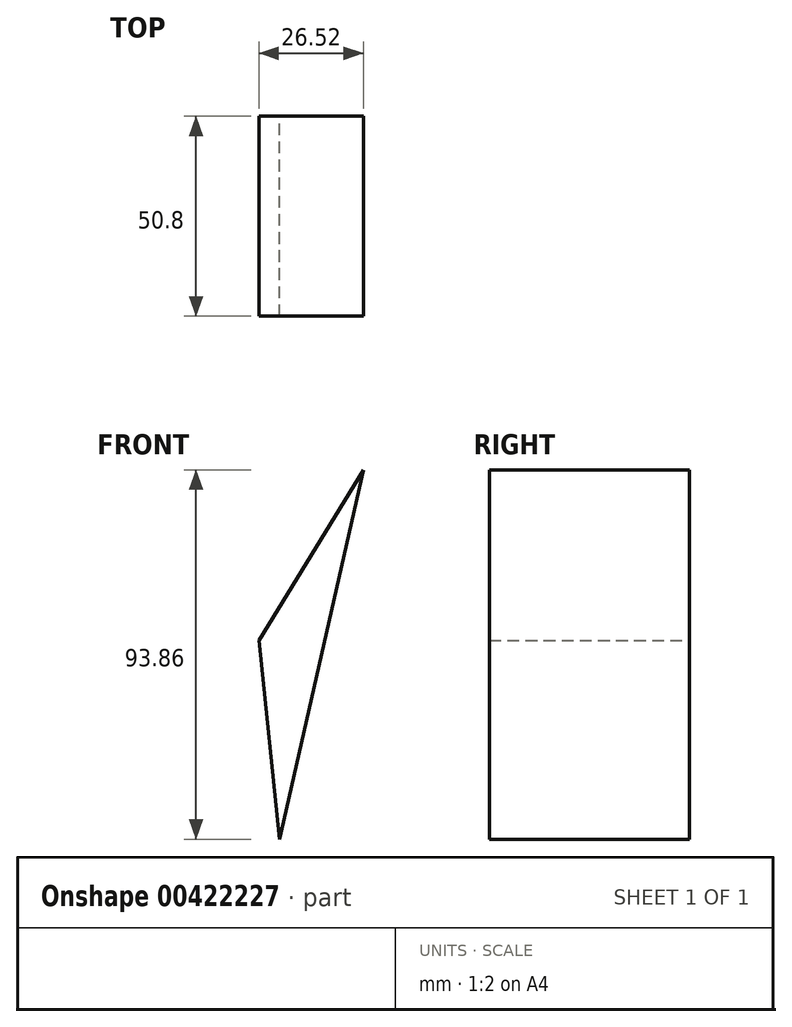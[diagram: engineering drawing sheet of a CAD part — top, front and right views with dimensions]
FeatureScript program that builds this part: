
annotation { "Feature Type Name" : "Feature", "Feature Type Description" : "" }
export const myFeature = defineFeature(function(context is Context, id is Id, definition is map)
    precondition{}
    {
        {
            var Q0;
            Q0=qCreatedBy(makeId("Front.planeOp"),FACE);
            var sketch = newSketch(context, id + "F0", { "sketchPlane" : qUnion([Q0])});
            skLineSegment(sketch, "E0", {"start": v(0, 58.67) * mm, "end": v(-26.52, 15.34) * mm});
            skLineSegment(sketch, "E1", {"start": v(-26.52, 15.34) * mm, "end": v(-21.34, -35.2) * mm});
            skLineSegment(sketch, "E2", {"start": v(-21.34, -35.2) * mm, "end": v(0, 58.67) * mm});
            skSolve(sketch);
        }
        {
            var Q0;
            Q0 = qSketchRegion(id + "F0", true);
            extrude(context, id + "F1", {"entities" : qUnion([Q0]), "depth" : 50.8 * mm});
        }
    });
